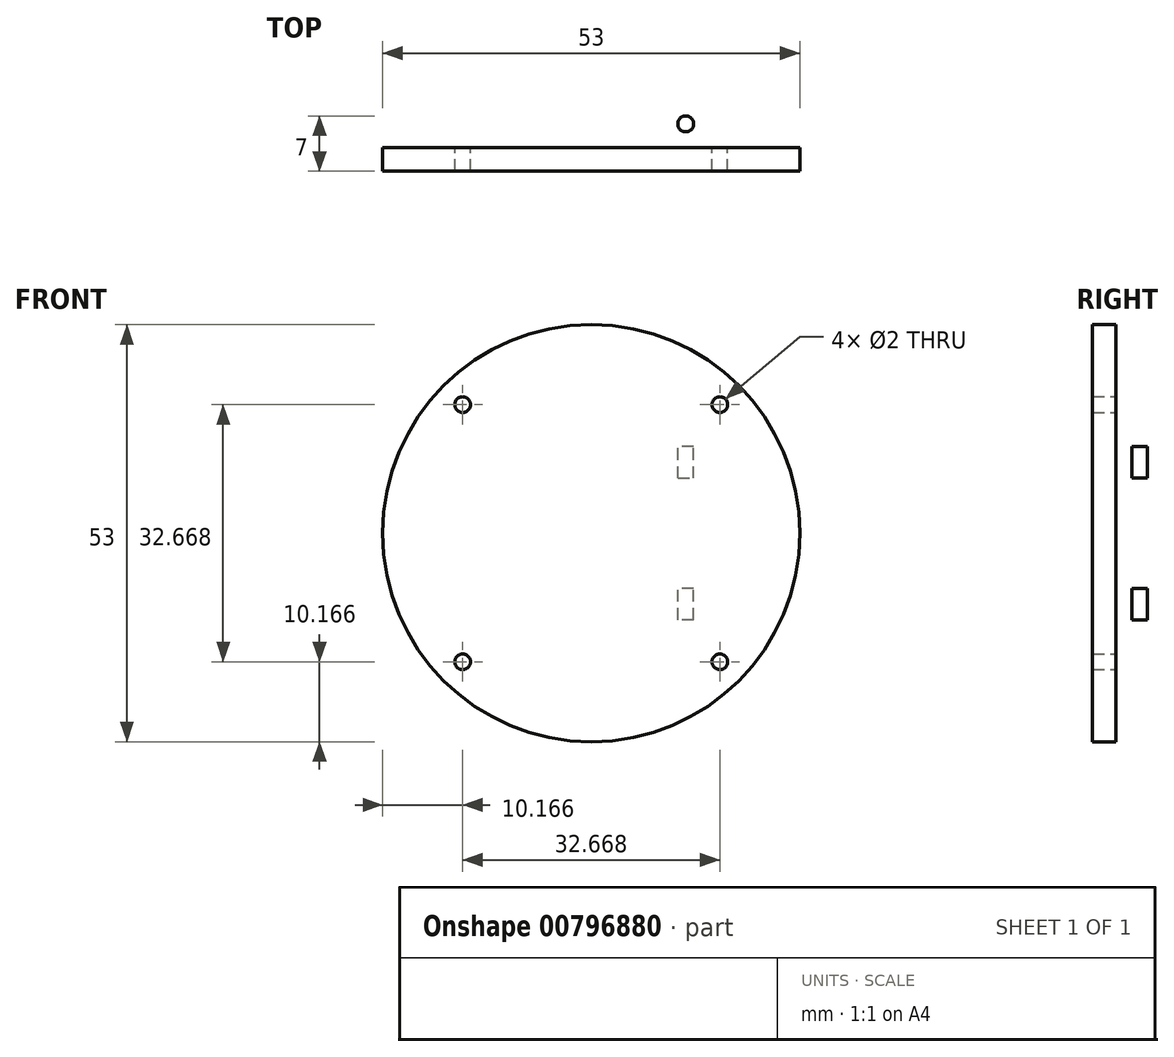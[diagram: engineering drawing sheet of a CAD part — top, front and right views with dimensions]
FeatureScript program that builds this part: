
annotation { "Feature Type Name" : "Feature", "Feature Type Description" : "" }
export const myFeature = defineFeature(function(context is Context, id is Id, definition is map)
    precondition{}
    {
        {
            var Q0;
            Q0=qCreatedBy(makeId("Front.planeOp"),FACE);
            var sketch = newSketch(context, id + "F0", { "sketchPlane" : qUnion([Q0])});
            skCircle(sketch, "E0", {"center": v(0, 0) * mm, "radius": 26.5 * mm});
            skCircle(sketch, "E1", {"center": v(0, 0) * mm, "radius": 23.1 * mm, "construction": true});
            skLineSegment(sketch, "E2", {"start": v(0, 0) * mm, "end": v(0, -39.34) * mm, "construction": true});
            skLineSegment(sketch, "E3", {"start": v(0, 0) * mm, "end": v(0, 41.95) * mm, "construction": true});
            skLineSegment(sketch, "E4", {"start": v(0, 0) * mm, "end": v(-31.01, 0) * mm, "construction": true});
            skLineSegment(sketch, "E5", {"start": v(0, 0) * mm, "end": v(34.75, 0) * mm, "construction": true});
            skLineSegment(sketch, "E6", {"start": v(0, 0) * mm, "end": v(-26.75, -26.75) * mm, "construction": true});
            skLineSegment(sketch, "E7", {"start": v(0, 0) * mm, "end": v(-34.89, 34.89) * mm, "construction": true});
            skLineSegment(sketch, "E8", {"start": v(0, 0) * mm, "end": v(33.63, 33.63) * mm, "construction": true});
            skLineSegment(sketch, "E9", {"start": v(0, 0) * mm, "end": v(35.16, -35.16) * mm, "construction": true});
            skCircle(sketch, "E10", {"center": v(16.33, -16.33) * mm, "radius": 1 * mm});
            skCircle(sketch, "E11", {"center": v(-16.33, -16.33) * mm, "radius": 1 * mm});
            skCircle(sketch, "E12", {"center": v(-16.33, 16.33) * mm, "radius": 1 * mm});
            skCircle(sketch, "E13", {"center": v(16.33, 16.33) * mm, "radius": 1 * mm});
            skLineSegment(sketch, "E14.bottom", {"start": v(0, 7) * mm, "end": v(21, 7) * mm});
            skLineSegment(sketch, "E14.top", {"start": v(0, 11) * mm, "end": v(21, 11) * mm});
            skLineSegment(sketch, "E14.left", {"start": v(0, 7) * mm, "end": v(0, 11) * mm});
            skLineSegment(sketch, "E14.right", {"start": v(21, 7) * mm, "end": v(21, 11) * mm});
            skLineSegment(sketch, "E15.MirrorCS", {"start": v(-21, 7) * mm, "end": v(-21, 11) * mm});
            skLineSegment(sketch, "E16.MirrorCS", {"start": v(0, 11) * mm, "end": v(-21, 11) * mm});
            skLineSegment(sketch, "E17.MirrorCS", {"start": v(0, 7) * mm, "end": v(-21, 7) * mm});
            skSolve(sketch);
        }
        {
            var Q0;
            Q0=makeQuery(id+"F0.imprint","IMPRINT",FACE,{"disambiguationData":[TD([[makeQuery(id+"F0.imprint","IMPRINT",EDGE,{"derivedFrom":sQuery(id+"F0.wireOp",EDGE,"E14.bottom")}),1.0]])]});
            var Q1;
            Q1=makeQuery(id+"F0.imprint","IMPRINT",FACE,{"disambiguationData":[TD([[makeQuery(id+"F0.imprint","IMPRINT",EDGE,{"derivedFrom":sQuery(id+"F0.wireOp",EDGE,"E14.left")}),1.0]])]});
            var Q2;
            Q2=makeQuery(id+"F0.imprint","IMPRINT",FACE,{"disambiguationData":[TD([[makeQuery(id+"F0.imprint","IMPRINT",EDGE,{"derivedFrom":sQuery(id+"F0.wireOp",EDGE,"E0")}),1.0]])]});
            extrude(context, id + "F1", {"entities" : qUnion([Q0, Q1, Q2]), "depth" : 3 * mm, "offsetDistance" : 25 * mm});
        }
        {
            var Q0;
            Q0=makeQuery(id+"F0.imprint","IMPRINT",FACE,{"disambiguationData":[TD([[makeQuery(id+"F0.imprint","IMPRINT",EDGE,{"derivedFrom":sQuery(id+"F0.wireOp",EDGE,"E14.bottom")}),1.0]])]});
            var Q1;
            Q1=makeQuery(id+"F0.imprint","IMPRINT",FACE,{"disambiguationData":[TD([[makeQuery(id+"F0.imprint","IMPRINT",EDGE,{"derivedFrom":sQuery(id+"F0.wireOp",EDGE,"E14.left")}),1.0]])]});
            extrude(context, id + "F2", {"entities" : qUnion([Q0, Q1]), "operationType" : NewBodyOperationType.ADD, "oppositeDirection" : true, "depth" : 10 * mm, "offsetDistance" : 25 * mm});
        }
        {
            var Q0;
            Q0=makeQuery(id+"F1.opExtrude","SWEPT_BODY",BODY,{"disambiguationData":[OSD([sQuery(id+"F0.wireOp",EDGE,"E0"),sQuery(id+"F0.wireOp",EDGE,"E10"),sQuery(id+"F0.wireOp",EDGE,"E11"),sQuery(id+"F0.wireOp",EDGE,"E12"),sQuery(id+"F0.wireOp",EDGE,"E13")])]});
            var Q1;
            Q1=qCreatedBy(makeId("Top.planeOp"),FACE);
            mirror(context, id + "F3", {"operationType" : NewBodyOperationType.ADD, "entities" : qUnion([Q0]), "mirrorPlane" : qUnion([Q1])});
        }
        {
            var Q0;
            Q0=makeQuery(id+"F2.opExtrude","SWEPT_FACE",FACE,{"disambiguationData":[OSD([sQuery(id+"F0.wireOp",EDGE,"E14.top"),sQuery(id+"F0.wireOp",EDGE,"E16.MirrorCS")])]});
            var sketch = newSketch(context, id + "F4", { "sketchPlane" : qUnion([Q0])});
            skLineSegment(sketch, "E18", {"start": v(-21, 3) * mm, "end": v(21, 3) * mm, "construction": true});
            skCircle(sketch, "E19", {"center": v(-12, 3) * mm, "radius": 1 * mm});
            skLineSegment(sketch, "E20", {"start": v(0, 0) * mm, "end": v(0, 15.1) * mm, "construction": true});
            skPoint(sketch, "E20.endSnap0", {"position": v(0, 10) * mm});
            skCircle(sketch, "E21.MirrorC", {"center": v(12, 3) * mm, "radius": 1 * mm});
            skSolve(sketch);
        }
        {
            var Q0;
            Q0=makeQuery(id+"F4.imprint","IMPRINT",FACE,{"disambiguationData":[TD([[makeQuery(id+"F4.imprint","IMPRINT",EDGE,{"derivedFrom":sQuery(id+"F4.wireOp",EDGE,"E19")}),1.0]])]});
            var Q1;
            Q1=makeQuery(id+"F4.imprint","IMPRINT",FACE,{"disambiguationData":[TD([[makeQuery(id+"F4.imprint","IMPRINT",EDGE,{"derivedFrom":sQuery(id+"F4.wireOp",EDGE,"E21.MirrorC")}),-1.0]])]});
            extrude(context, id + "F5", {"entities" : qUnion([Q0, Q1]), "operationType" : NewBodyOperationType.REMOVE, "endBound" : BoundingType.THROUGH_ALL, "oppositeDirection" : true, "depth" : 25 * mm, "offsetDistance" : 25 * mm});
        }
    });
